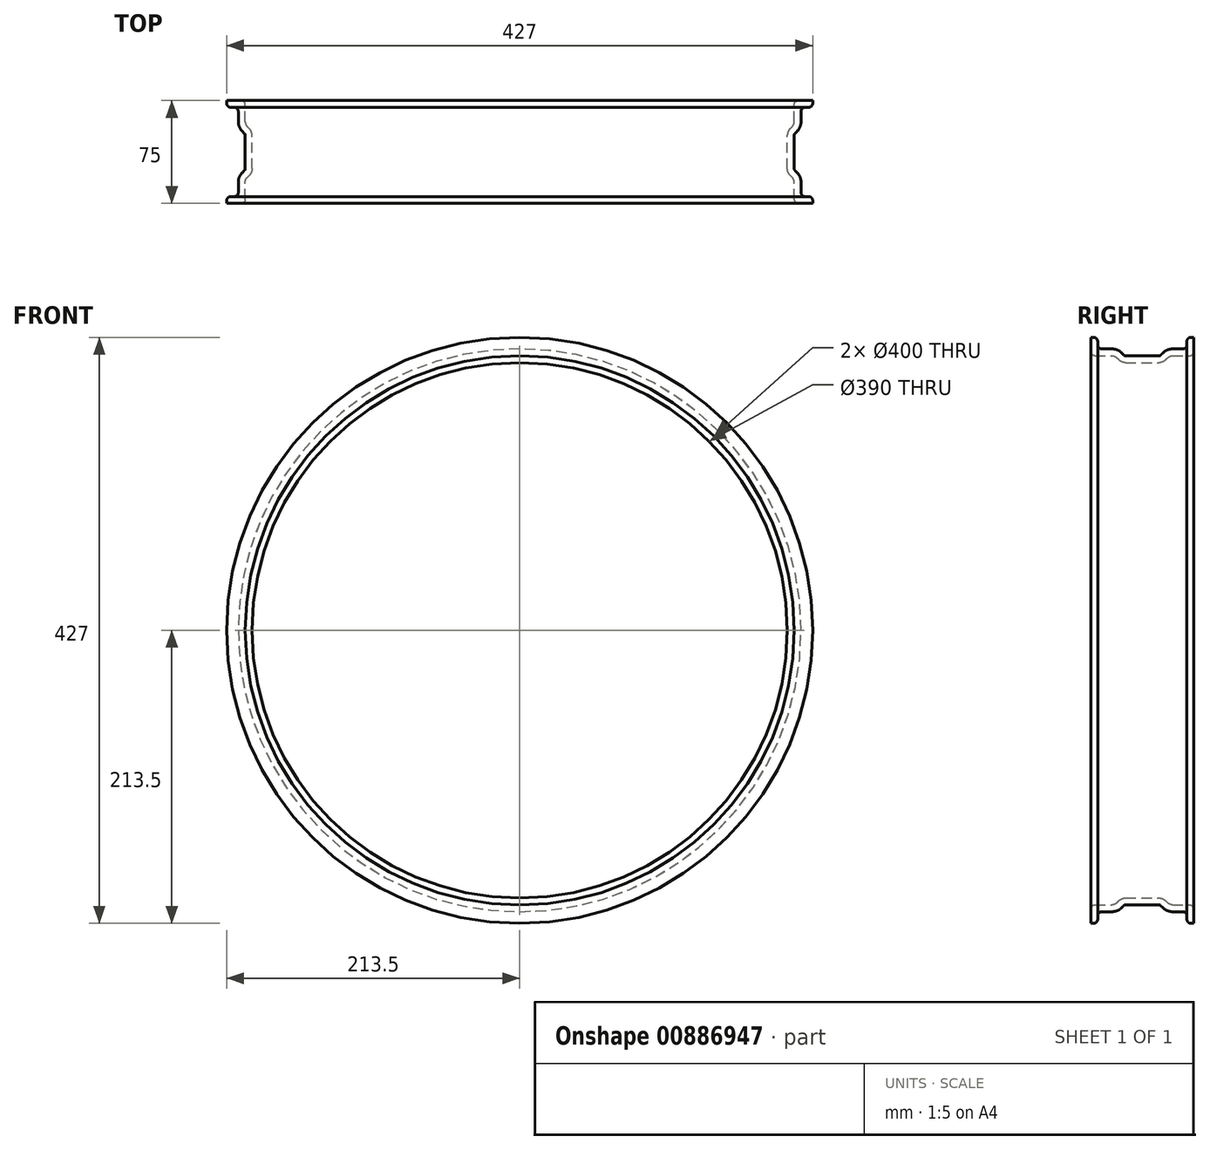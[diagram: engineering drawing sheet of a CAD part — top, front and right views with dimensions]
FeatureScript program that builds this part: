
annotation { "Feature Type Name" : "Feature", "Feature Type Description" : "" }
export const myFeature = defineFeature(function(context is Context, id is Id, definition is map)
    precondition{}
    {
        {
            var Q0;
            Q0=qCreatedBy(makeId("Front.planeOp"),FACE);
            var sketch = newSketch(context, id + "F0", { "sketchPlane" : qUnion([Q0])});
            skCircle(sketch, "E0", {"center": v(0, 0) * mm, "radius": 195 * mm});
            skCircle(sketch, "E1", {"center": v(0, 0) * mm, "radius": 200 * mm});
            skCircle(sketch, "E2", {"center": v(0, 0) * mm, "radius": 203.5 * mm});
            skCircle(sketch, "E3", {"center": v(0, 0) * mm, "radius": 213.5 * mm});
            skSolve(sketch);
        }
        {
            var Q0;
            Q0=makeQuery(id+"F0.imprint","IMPRINT",FACE,{"disambiguationData":[TD([[makeQuery(id+"F0.imprint","IMPRINT",EDGE,{"derivedFrom":sQuery(id+"F0.wireOp",EDGE,"E2")}),-1.0]])]});
            extrude(context, id + "F1", {"entities" : qUnion([Q0]), "endBound" : BoundingType.SYMMETRIC, "depth" : 75 * mm, "offsetDistance" : 25 * mm});
        }
        {
            var Q0;
            Q0=makeQuery(id+"F0.imprint","IMPRINT",FACE,{"disambiguationData":[TD([[makeQuery(id+"F0.imprint","IMPRINT",EDGE,{"derivedFrom":sQuery(id+"F0.wireOp",EDGE,"E1")}),-1.0]])]});
            extrude(context, id + "F2", {"entities" : qUnion([Q0]), "operationType" : NewBodyOperationType.ADD, "endBound" : BoundingType.SYMMETRIC, "depth" : 75 * mm, "offsetDistance" : 25 * mm});
        }
        {
            var Q0;
            Q0=makeQuery(id+"F0.imprint","IMPRINT",FACE,{"disambiguationData":[TD([[makeQuery(id+"F0.imprint","IMPRINT",EDGE,{"derivedFrom":sQuery(id+"F0.wireOp",EDGE,"E0")}),-1.0]])]});
            extrude(context, id + "F3", {"entities" : qUnion([Q0]), "operationType" : NewBodyOperationType.ADD, "endBound" : BoundingType.SYMMETRIC, "depth" : 40 * mm, "offsetDistance" : 25 * mm});
        }
        {
            var Q0;
            Q0=makeQuery(id+"F2.opExtrude","CAP_EDGE",EDGE,{"disambiguationData":[OSD([sQuery(id+"F0.wireOp",EDGE,"E1")])],"isStart":false});
            var Q1;
            Q1=makeQuery(id+"F2.opExtrude","CAP_EDGE",EDGE,{"disambiguationData":[OSD([sQuery(id+"F0.wireOp",EDGE,"E1")])],"isStart":true});
            fillet(context, id + "F4", {"entities" : qUnion([Q0, Q1]), "radius" : 3 * mm, "tangentPropagation" : true, "allowEdgeOverflow" : false});
        }
        {
            var Q0;
            Q0=makeQuery(id+"F3.opExtrude","CAP_EDGE",EDGE,{"disambiguationData":[OSD([sQuery(id+"F0.wireOp",EDGE,"E0")])],"isStart":false});
            var Q1;
            Q1=makeQuery(id+"F3.opExtrude","CAP_EDGE",EDGE,{"disambiguationData":[OSD([sQuery(id+"F0.wireOp",EDGE,"E0")])],"isStart":true});
            chamfer(context, id + "F5", {"entities" : qUnion([Q0, Q1]), "width" : 5 * mm, "tangentPropagation" : true});
        }
        {
            var Q0;
            {var subQ0=sQuery(id+"F0.wireOp",EDGE,"E2");var subQ1=sQuery(id+"F0.wireOp",EDGE,"E1");var subQ2=sQuery(id+"F0.wireOp",EDGE,"E0");Q0=makeQuery(id+"F5.opChamfer","BLEND_EDGE",EDGE,{"blendedFrom":[makeQuery(id+"F3.opExtrude","CAP_EDGE",EDGE,{"disambiguationData":[OSD([subQ2])],"isStart":false}),makeQuery(id+"F3.boolean.opBoolean","SPLIT",FACE,{"disambiguationData":[TD([makeQuery(id+"F1.opExtrude","CAP_FACE",FACE,{"disambiguationData":[OSD([subQ0,sQuery(id+"F0.wireOp",EDGE,"E3")])],"isStart":false})])],"derivedFrom":makeQuery(id+"F2.opExtrude","SWEPT_FACE",FACE,{"disambiguationData":[OSD([subQ1])]})})],"blendedInto":[makeQuery(id+"F3.boolean.opBoolean","SPLIT",FACE,{"disambiguationData":[TD([makeQuery(id+"F1.opExtrude","CAP_FACE",FACE,{"disambiguationData":[OSD([subQ0,sQuery(id+"F0.wireOp",EDGE,"E3")])],"isStart":false})])],"derivedFrom":makeQuery(id+"F2.opExtrude","SWEPT_FACE",FACE,{"disambiguationData":[OSD([subQ1])]})})]});}
            var Q1;
            {var subQ0=sQuery(id+"F0.wireOp",EDGE,"E2");var subQ1=sQuery(id+"F0.wireOp",EDGE,"E1");var subQ2=sQuery(id+"F0.wireOp",EDGE,"E0");Q1=makeQuery(id+"F5.opChamfer","BLEND_EDGE",EDGE,{"blendedFrom":[makeQuery(id+"F3.opExtrude","CAP_EDGE",EDGE,{"disambiguationData":[OSD([subQ2])],"isStart":true}),makeQuery(id+"F3.boolean.opBoolean","SPLIT",FACE,{"disambiguationData":[TD([makeQuery(id+"F1.opExtrude","CAP_FACE",FACE,{"disambiguationData":[OSD([subQ0,sQuery(id+"F0.wireOp",EDGE,"E3")])],"isStart":true})])],"derivedFrom":makeQuery(id+"F2.opExtrude","SWEPT_FACE",FACE,{"disambiguationData":[OSD([subQ1])]})})],"blendedInto":[makeQuery(id+"F3.boolean.opBoolean","SPLIT",FACE,{"disambiguationData":[TD([makeQuery(id+"F1.opExtrude","CAP_FACE",FACE,{"disambiguationData":[OSD([subQ0,sQuery(id+"F0.wireOp",EDGE,"E3")])],"isStart":true})])],"derivedFrom":makeQuery(id+"F2.opExtrude","SWEPT_FACE",FACE,{"disambiguationData":[OSD([subQ1])]})})]});}
            fillet(context, id + "F6", {"entities" : qUnion([Q0, Q1]), "radius" : 5 * mm, "tangentPropagation" : true, "allowEdgeOverflow" : false});
        }
        {
            var Q0;
            {var subQ0=sQuery(id+"F0.wireOp",EDGE,"E0");Q0=makeQuery(id+"F5.opChamfer","BLEND_EDGE",EDGE,{"blendedFrom":[makeQuery(id+"F3.opExtrude","CAP_EDGE",EDGE,{"disambiguationData":[OSD([subQ0])],"isStart":true}),makeQuery(id+"F3.opExtrude","SWEPT_FACE",FACE,{"disambiguationData":[OSD([subQ0])]})],"blendedInto":[makeQuery(id+"F3.opExtrude","SWEPT_FACE",FACE,{"disambiguationData":[OSD([subQ0])]})]});}
            var Q1;
            {var subQ0=sQuery(id+"F0.wireOp",EDGE,"E0");Q1=makeQuery(id+"F5.opChamfer","BLEND_EDGE",EDGE,{"blendedFrom":[makeQuery(id+"F3.opExtrude","CAP_EDGE",EDGE,{"disambiguationData":[OSD([subQ0])],"isStart":false}),makeQuery(id+"F3.opExtrude","SWEPT_FACE",FACE,{"disambiguationData":[OSD([subQ0])]})],"blendedInto":[makeQuery(id+"F3.opExtrude","SWEPT_FACE",FACE,{"disambiguationData":[OSD([subQ0])]})]});}
            fillet(context, id + "F7", {"entities" : qUnion([Q0, Q1]), "radius" : 7 * mm, "tangentPropagation" : true, "allowEdgeOverflow" : false});
        }
        {
            var Q0;
            Q0=makeQuery(id+"F1.opExtrude","SWEPT_FACE",FACE,{"disambiguationData":[OSD([sQuery(id+"F0.wireOp",EDGE,"E3")])]});
            shell(context, id + "F8", {"entities" : qUnion([Q0]), "thickness" : 5 * mm});
        }
        {
            var Q0;
            {var subQ0=sQuery(id+"F0.wireOp",EDGE,"E3");Q0=makeQuery(id+"F8.opShell","OFFSET_EDGE",EDGE,{"disambiguationData":[OSD([subQ0]),TDD([makeQuery(id+"F1.opExtrude","CAP_EDGE",EDGE,{"disambiguationData":[OSD([subQ0])],"isStart":true})])]});}
            var Q1;
            {var subQ0=sQuery(id+"F0.wireOp",EDGE,"E3");Q1=makeQuery(id+"F8.opShell","OFFSET_EDGE",EDGE,{"disambiguationData":[OSD([subQ0]),TDD([makeQuery(id+"F1.opExtrude","CAP_EDGE",EDGE,{"disambiguationData":[OSD([subQ0])],"isStart":false})])]});}
            var Q2;
            {var subQ0=sQuery(id+"F0.wireOp",EDGE,"E3");var subQ1=sQuery(id+"F0.wireOp",EDGE,"E2");var subQ2=makeQuery(id+"F1.opExtrude","CAP_FACE",FACE,{"disambiguationData":[OSD([subQ1,subQ0])],"isStart":false});var subQ3=sQuery(id+"F0.wireOp",EDGE,"E1");var subQ4=makeQuery(id+"F2.opExtrude","CAP_FACE",FACE,{"disambiguationData":[OSD([subQ3,subQ1])],"isStart":false});var subQ5=makeQuery(id+"F2.opExtrude","CAP_EDGE",EDGE,{"disambiguationData":[OSD([subQ3])],"isStart":false});Q2=makeQuery(id+"F8.opShell","OFFSET_EDGE",EDGE,{"disambiguationData":[OSD([subQ3,subQ1,subQ0]),TDD([makeQuery(id+"F4.opFillet","BLEND_EDGE",EDGE,{"blendedFrom":[subQ5,makeQuery(id+"F2.boolean.opBoolean","MERGE",FACE,{"derivedFrom":[subQ2,subQ4]})],"blendedInto":[makeQuery(id+"F2.boolean.opBoolean","MERGE",FACE,{"derivedFrom":[subQ2,subQ4]})]}),makeQuery(id+"F4.opFillet","BLEND_EDGE",EDGE,{"blendedFrom":[subQ5,makeQuery(id+"F3.boolean.opBoolean","SPLIT",FACE,{"disambiguationData":[TD([subQ2])],"derivedFrom":makeQuery(id+"F2.opExtrude","SWEPT_FACE",FACE,{"disambiguationData":[OSD([subQ3])]})})],"blendedInto":[makeQuery(id+"F3.boolean.opBoolean","SPLIT",FACE,{"disambiguationData":[TD([subQ2])],"derivedFrom":makeQuery(id+"F2.opExtrude","SWEPT_FACE",FACE,{"disambiguationData":[OSD([subQ3])]})})]})])]});}
            var Q3;
            {var subQ0=sQuery(id+"F0.wireOp",EDGE,"E3");var subQ1=sQuery(id+"F0.wireOp",EDGE,"E2");var subQ2=makeQuery(id+"F1.opExtrude","CAP_FACE",FACE,{"disambiguationData":[OSD([subQ1,subQ0])],"isStart":true});var subQ3=sQuery(id+"F0.wireOp",EDGE,"E1");var subQ4=makeQuery(id+"F2.opExtrude","CAP_FACE",FACE,{"disambiguationData":[OSD([subQ3,subQ1])],"isStart":true});var subQ5=makeQuery(id+"F2.opExtrude","CAP_EDGE",EDGE,{"disambiguationData":[OSD([subQ3])],"isStart":true});Q3=makeQuery(id+"F8.opShell","OFFSET_EDGE",EDGE,{"disambiguationData":[OSD([subQ3,subQ1,subQ0]),TDD([makeQuery(id+"F4.opFillet","BLEND_EDGE",EDGE,{"blendedFrom":[subQ5,makeQuery(id+"F2.boolean.opBoolean","MERGE",FACE,{"derivedFrom":[subQ2,subQ4]})],"blendedInto":[makeQuery(id+"F2.boolean.opBoolean","MERGE",FACE,{"derivedFrom":[subQ2,subQ4]})]}),makeQuery(id+"F4.opFillet","BLEND_EDGE",EDGE,{"blendedFrom":[subQ5,makeQuery(id+"F3.boolean.opBoolean","SPLIT",FACE,{"disambiguationData":[TD([subQ2])],"derivedFrom":makeQuery(id+"F2.opExtrude","SWEPT_FACE",FACE,{"disambiguationData":[OSD([subQ3])]})})],"blendedInto":[makeQuery(id+"F3.boolean.opBoolean","SPLIT",FACE,{"disambiguationData":[TD([subQ2])],"derivedFrom":makeQuery(id+"F2.opExtrude","SWEPT_FACE",FACE,{"disambiguationData":[OSD([subQ3])]})})]})])]});}
            fillet(context, id + "F9", {"entities" : qUnion([Q0, Q1, Q2, Q3]), "radius" : 3 * mm, "tangentPropagation" : true, "allowEdgeOverflow" : false});
        }
    });
